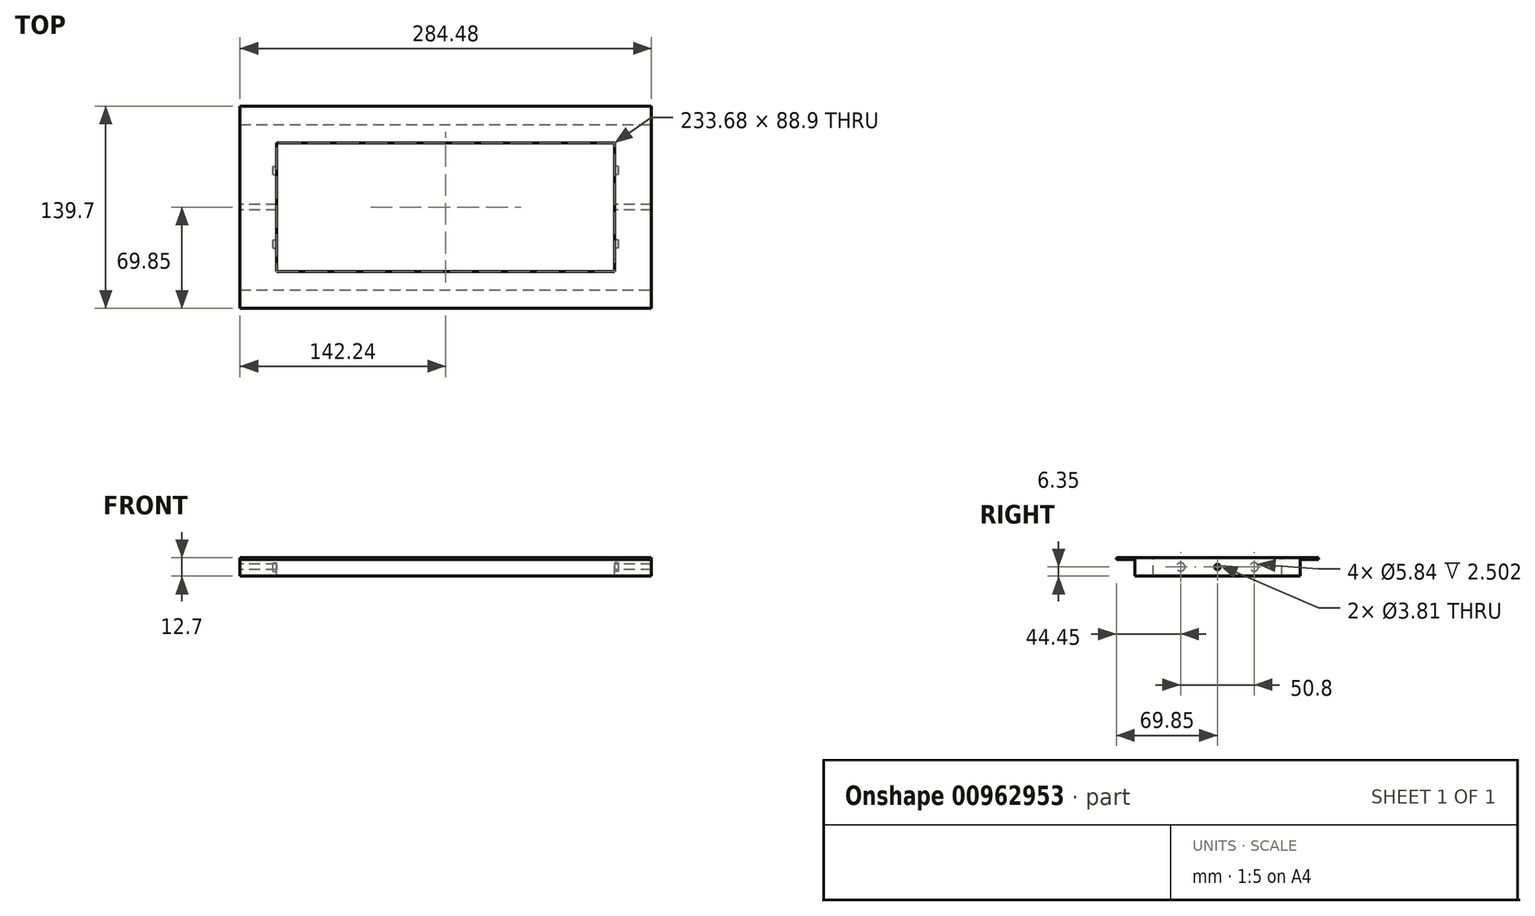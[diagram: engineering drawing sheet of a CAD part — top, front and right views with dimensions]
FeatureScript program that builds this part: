
annotation { "Feature Type Name" : "Feature", "Feature Type Description" : "" }
export const myFeature = defineFeature(function(context is Context, id is Id, definition is map)
    precondition{}
    {
        {
            var Q0;
            Q0=qCreatedBy(makeId("Top.planeOp"),FACE);
            var sketch = newSketch(context, id + "F0", { "sketchPlane" : qUnion([Q0])});
            skLineSegment(sketch, "E0.bottom", {"start": v(-142.24, 69.85) * mm, "end": v(142.24, 69.85) * mm});
            skLineSegment(sketch, "E0.top", {"start": v(-142.24, -69.85) * mm, "end": v(142.24, -69.85) * mm});
            skLineSegment(sketch, "E0.left", {"start": v(-142.24, 69.85) * mm, "end": v(-142.24, -69.85) * mm});
            skLineSegment(sketch, "E0.right", {"start": v(142.24, 69.85) * mm, "end": v(142.24, -69.85) * mm});
            skPoint(sketch, "E0.middle", {"position": v(0, 0) * mm});
            skSolve(sketch);
        }
        {
            var Q0;
            Q0 = qSketchRegion(id + "F0", true);
            extrude(context, id + "F1", {"entities" : qUnion([Q0]), "depth" : 12.7 * mm, "offsetDistance" : 25.4 * mm});
        }
        {
            var Q0;
            Q0=makeQuery(id+"F1.opExtrude","CAP_FACE",FACE,{"disambiguationData":[OSD([sQuery(id+"F0.wireOp",EDGE,"E0.bottom"),sQuery(id+"F0.wireOp",EDGE,"E0.top"),sQuery(id+"F0.wireOp",EDGE,"E0.left"),sQuery(id+"F0.wireOp",EDGE,"E0.right")])],"isStart":false});
            var sketch = newSketch(context, id + "F2", { "sketchPlane" : qUnion([Q0])});
            skLineSegment(sketch, "E1.bottom", {"start": v(-116.84, 44.45) * mm, "end": v(116.84, 44.45) * mm});
            skLineSegment(sketch, "E1.top", {"start": v(-116.84, -44.45) * mm, "end": v(116.84, -44.45) * mm});
            skLineSegment(sketch, "E1.left", {"start": v(-116.84, 44.45) * mm, "end": v(-116.84, -44.45) * mm});
            skLineSegment(sketch, "E1.right", {"start": v(116.84, 44.45) * mm, "end": v(116.84, -44.45) * mm});
            skPoint(sketch, "E1.middle", {"position": v(0, 0) * mm});
            skSolve(sketch);
        }
        {
            var Q0;
            Q0 = qSketchRegion(id + "F2", true);
            extrude(context, id + "F3", {"entities" : qUnion([Q0]), "operationType" : NewBodyOperationType.REMOVE, "oppositeDirection" : true, "depth" : 25.4 * mm, "offsetDistance" : 25.4 * mm});
        }
        {
            var Q0;
            Q0=makeQuery(id+"F1.opExtrude","SWEPT_FACE",FACE,{"disambiguationData":[OSD([sQuery(id+"F0.wireOp",EDGE,"E0.left")])]});
            var sketch = newSketch(context, id + "F4", { "sketchPlane" : qUnion([Q0])});
            skCircle(sketch, "E2", {"center": v(0, 6.35) * mm, "radius": 1.9 * mm});
            skSolve(sketch);
        }
        {
            var Q0;
            Q0 = qSketchRegion(id + "F4", true);
            extrude(context, id + "F5", {"entities" : qUnion([Q0]), "operationType" : NewBodyOperationType.REMOVE, "oppositeDirection" : true, "depth" : 508 * mm, "offsetDistance" : 25.4 * mm});
        }
        {
            var Q0;
            Q0=makeQuery(id+"F3.boolean.opBoolean","COPY",FACE,{"derivedFrom":makeQuery(id+"F3.opExtrude","SWEPT_FACE",FACE,{"disambiguationData":[OSD([sQuery(id+"F2.wireOp",EDGE,"E1.left")])]})});
            var sketch = newSketch(context, id + "F6", { "sketchPlane" : qUnion([Q0])});
            skLineSegment(sketch, "E3.bottom", {"start": v(50.8, 12.7) * mm, "end": v(-50.8, 12.7) * mm});
            skLineSegment(sketch, "E3.top", {"start": v(50.8, 0) * mm, "end": v(-50.8, 0) * mm});
            skLineSegment(sketch, "E3.left", {"start": v(50.8, 12.7) * mm, "end": v(50.8, 0) * mm});
            skLineSegment(sketch, "E3.right", {"start": v(-50.8, 12.7) * mm, "end": v(-50.8, 0) * mm});
            skPoint(sketch, "E3.middle", {"position": v(0, 6.35) * mm});
            skCircle(sketch, "E4", {"center": v(-25.4, 6.35) * mm, "radius": 2.92 * mm});
            skCircle(sketch, "E5", {"center": v(25.4, 6.35) * mm, "radius": 2.92 * mm});
            skSolve(sketch);
        }
        {
            var Q0;
            Q0=makeQuery(id+"F6.imprint","IMPRINT",FACE,{"disambiguationData":[TD([[makeQuery(id+"F6.imprint","IMPRINT",EDGE,{"derivedFrom":sQuery(id+"F6.wireOp",EDGE,"E4")}),1.0]])]});
            var Q1;
            Q1=makeQuery(id+"F6.imprint","IMPRINT",FACE,{"disambiguationData":[TD([[makeQuery(id+"F6.imprint","IMPRINT",EDGE,{"derivedFrom":sQuery(id+"F6.wireOp",EDGE,"E5")}),1.0]])]});
            extrude(context, id + "F7", {"entities" : qUnion([Q0, Q1]), "operationType" : NewBodyOperationType.REMOVE, "oppositeDirection" : true, "depth" : 2.5 * mm, "offsetDistance" : 25.4 * mm});
        }
        {
            var Q0;
            Q0=makeQuery(id+"F3.boolean.opBoolean","COPY",FACE,{"derivedFrom":makeQuery(id+"F3.opExtrude","SWEPT_FACE",FACE,{"disambiguationData":[OSD([sQuery(id+"F2.wireOp",EDGE,"E1.right")])]})});
            var sketch = newSketch(context, id + "F8", { "sketchPlane" : qUnion([Q0])});
            skLineSegment(sketch, "E6.bottom", {"start": v(-50.8, 12.7) * mm, "end": v(50.8, 12.7) * mm});
            skLineSegment(sketch, "E6.top", {"start": v(-50.8, 0) * mm, "end": v(50.8, 0) * mm});
            skLineSegment(sketch, "E6.left", {"start": v(-50.8, 12.7) * mm, "end": v(-50.8, 0) * mm});
            skLineSegment(sketch, "E6.right", {"start": v(50.8, 12.7) * mm, "end": v(50.8, 0) * mm});
            skPoint(sketch, "E6.middle", {"position": v(0, 6.35) * mm});
            skCircle(sketch, "E7", {"center": v(-25.4, 6.35) * mm, "radius": 2.92 * mm});
            skCircle(sketch, "E8", {"center": v(25.4, 6.35) * mm, "radius": 2.92 * mm});
            skSolve(sketch);
        }
        {
            var Q0;
            Q0=makeQuery(id+"F8.imprint","IMPRINT",FACE,{"disambiguationData":[TD([[makeQuery(id+"F8.imprint","IMPRINT",EDGE,{"derivedFrom":sQuery(id+"F8.wireOp",EDGE,"E7")}),1.0]])]});
            var Q1;
            Q1=makeQuery(id+"F8.imprint","IMPRINT",FACE,{"disambiguationData":[TD([[makeQuery(id+"F8.imprint","IMPRINT",EDGE,{"derivedFrom":sQuery(id+"F8.wireOp",EDGE,"E8")}),1.0]])]});
            extrude(context, id + "F9", {"entities" : qUnion([Q0, Q1]), "operationType" : NewBodyOperationType.REMOVE, "oppositeDirection" : true, "depth" : 2.5 * mm, "offsetDistance" : 25.4 * mm});
        }
        {
            var Q0;
            Q0=makeQuery(id+"F1.opExtrude","SWEPT_FACE",FACE,{"disambiguationData":[OSD([sQuery(id+"F0.wireOp",EDGE,"E0.right")])]});
            var sketch = newSketch(context, id + "F10", { "sketchPlane" : qUnion([Q0])});
            skLineSegment(sketch, "E9.bottom", {"start": v(-69.85, 12.7) * mm, "end": v(-57.15, 12.7) * mm});
            skLineSegment(sketch, "E9.top", {"start": v(-69.85, 0) * mm, "end": v(-57.15, 0) * mm});
            skLineSegment(sketch, "E9.left", {"start": v(-69.85, 12.7) * mm, "end": v(-69.85, 0) * mm});
            skLineSegment(sketch, "E9.right", {"start": v(-57.15, 12.7) * mm, "end": v(-57.15, 0) * mm});
            skLineSegment(sketch, "E10.top", {"start": v(-69.85, 11.43) * mm, "end": v(-57.15, 11.43) * mm});
            skLineSegment(sketch, "E10.left", {"start": v(-69.85, 0) * mm, "end": v(-69.85, 11.43) * mm});
            skLineSegment(sketch, "E10.right", {"start": v(-57.15, 0) * mm, "end": v(-57.15, 11.43) * mm});
            skSolve(sketch);
        }
        {
            var Q0;
            Q0=makeQuery(id+"F10.imprint","IMPRINT",FACE,{"disambiguationData":[TD([[makeQuery(id+"F10.imprint","IMPRINT",EDGE,{"derivedFrom":sQuery(id+"F10.wireOp",EDGE,"E9.top")}),-1.0]])]});
            extrude(context, id + "F11", {"entities" : qUnion([Q0]), "operationType" : NewBodyOperationType.REMOVE, "oppositeDirection" : true, "depth" : 508 * mm, "offsetDistance" : 25.4 * mm});
        }
        {
            var Q0;
            Q0=makeQuery(id+"F1.opExtrude","SWEPT_FACE",FACE,{"disambiguationData":[OSD([sQuery(id+"F0.wireOp",EDGE,"E0.right")])]});
            var sketch = newSketch(context, id + "F12", { "sketchPlane" : qUnion([Q0])});
            skLineSegment(sketch, "E11.bottom", {"start": v(69.85, 0) * mm, "end": v(57.15, 0) * mm});
            skLineSegment(sketch, "E11.top", {"start": v(69.85, 11.43) * mm, "end": v(57.15, 11.43) * mm});
            skLineSegment(sketch, "E11.left", {"start": v(69.85, 0) * mm, "end": v(69.85, 11.43) * mm});
            skLineSegment(sketch, "E11.right", {"start": v(57.15, 0) * mm, "end": v(57.15, 11.43) * mm});
            skSolve(sketch);
        }
        {
            var Q0;
            Q0 = qSketchRegion(id + "F12", true);
            extrude(context, id + "F13", {"entities" : qUnion([Q0]), "operationType" : NewBodyOperationType.REMOVE, "oppositeDirection" : true, "depth" : 508 * mm, "offsetDistance" : 25.4 * mm});
        }
    });
